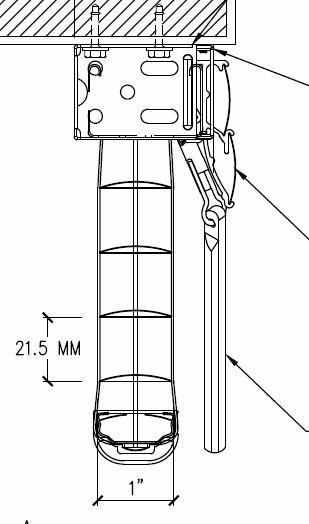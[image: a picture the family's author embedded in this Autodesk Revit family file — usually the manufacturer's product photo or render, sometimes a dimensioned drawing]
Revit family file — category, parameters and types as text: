
# Revit family: Window-Treatment_Pleated_SWFcontract_Pleated-Motorized
name_source: partatom
category: Specialty Equipment
units: mm (PartAtom-declared; Revit-internal decimal feet)

## family parameters
Always vertical = No
Classification Number = 23.30.60.14
Cut with Voids When Loaded = No
Enable Cutting in Views = No
Maintain Annotation Orientation = No
Part Type = Normal
Room Calculation Point = No
Round Connector Dimension = Use Diameter
Shared = No
Work Plane-Based = Yes

## types (2) — shared parameters
Assembly Code = E2010300
Cell Spacing = 0' - 1 1/4"
Construction Details = http://www.arcat.com
Default Elevation = 0' - 0"
Green Building-LEED = http://www.arcat.com
Header Depth = 0' - 2"
Header Height = 0' - 1 7/16"
Keynote = 12490
Large Single Cell Construction = No
Manufacturer = SWFcontract
Manufacturer Website = http://www.swfcontract.com
Product Data = http://www.arcat.com
Revision = R1_03-2014
Sales Information = http://www.swfcontract.com
Send Message = http://www.arcat.com
SpecWizard = http://www.arcat.com
Specification = http://www.arcat.com
URL = http://www.swfcontract.com
Unit Height = 4' - 0"
Unit Width = 4' - 0"
handlelength = 2' - 6"
zero-valued in all types: Expected Lifespan (Years), Maintenance Schedule (Months), Warranty Duration (Years)

## per-type parameters (varying)
| type | Description | Double Cell Construction | Model | Small Single Cell Construction |
| FashionPleat Motorized | SWFcontract Motorized Pleated Shade - Graber FashionPleat as Specified | No | Graber FashionPleat as Specified | Yes |
| EvenPleat Motorized | SWFcontract Motorized Pleated Shade - Graber EvenPleat as Specified | Yes | Graber EvenPleat as Specified | No |

## geometry (parser evidence)
native form markers: Blend x5, Sweep x4
no freeform markers — native parametric forms only
